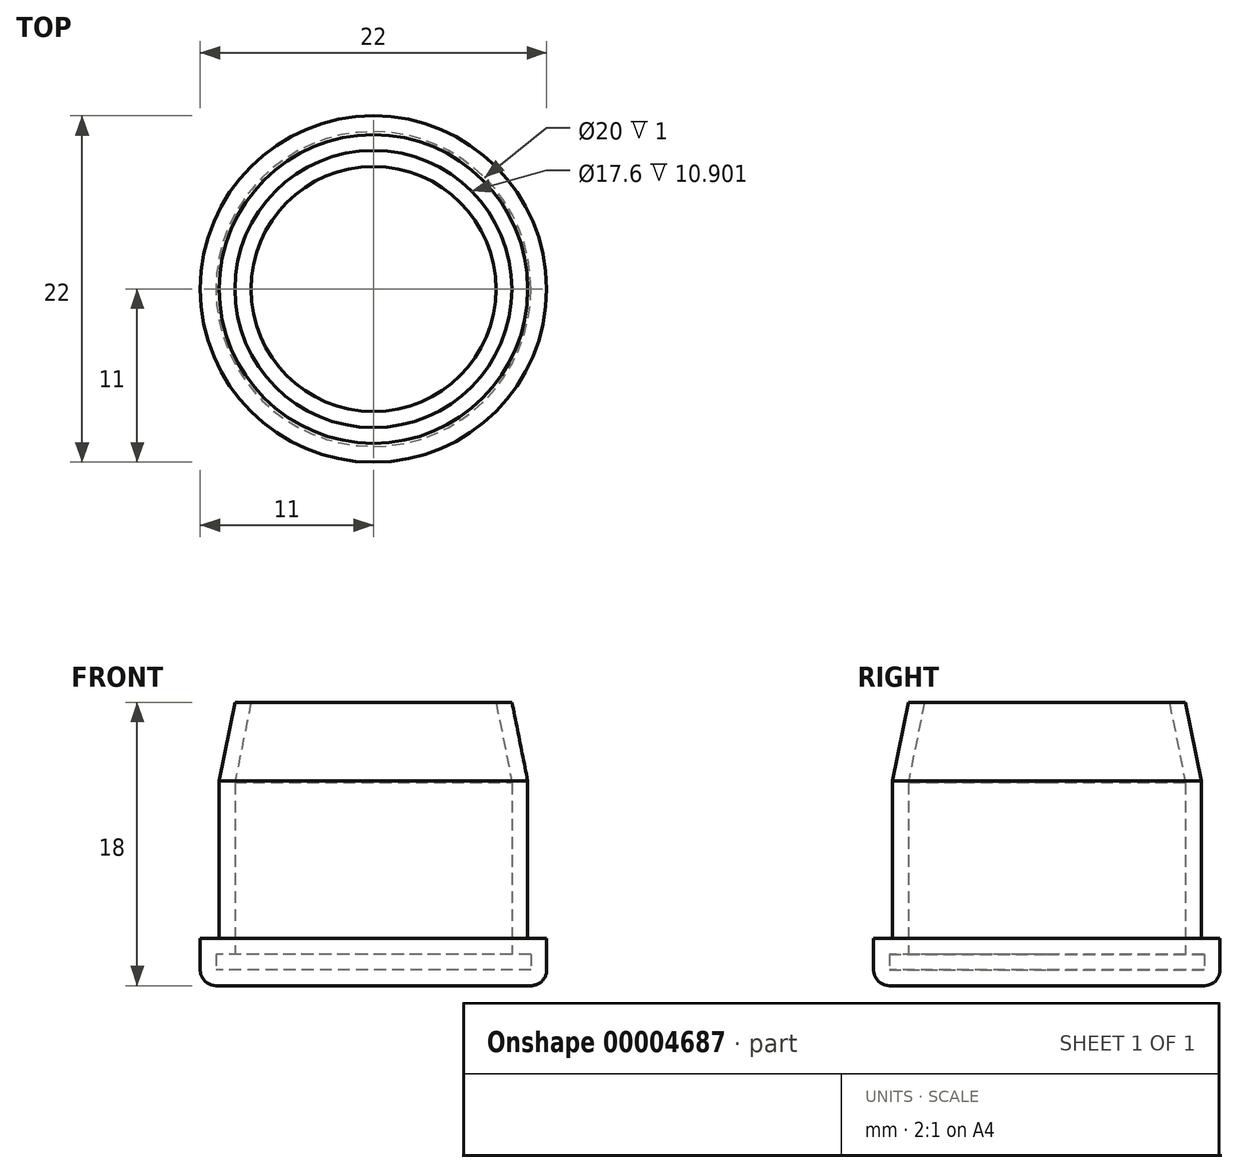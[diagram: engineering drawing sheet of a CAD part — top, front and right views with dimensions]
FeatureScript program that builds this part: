
annotation { "Feature Type Name" : "Feature", "Feature Type Description" : "" }
export const myFeature = defineFeature(function(context is Context, id is Id, definition is map)
    precondition{}
    {
        {
            var Q0;
            Q0=qCreatedBy(makeId("Top.planeOp"),FACE);
            var sketch = newSketch(context, id + "F0", { "sketchPlane" : qUnion([Q0])});
            skCircle(sketch, "E0", {"center": v(0, 0) * mm, "radius": 11 * mm});
            skSolve(sketch);
        }
        {
            var Q0;
            Q0 = qSketchRegion(id + "F0", true);
            extrude(context, id + "F1", {"entities" : qUnion([Q0]), "depth" : 3 * mm});
        }
        {
            var Q0;
            Q0=makeQuery(id+"F1.opExtrude","CAP_FACE",FACE,{"disambiguationData":[OSD([sQuery(id+"F0.wireOp",EDGE,"E0")])],"isStart":false});
            var sketch = newSketch(context, id + "F2", { "sketchPlane" : qUnion([Q0])});
            skCircle(sketch, "E1", {"center": v(0, 0) * mm, "radius": 9.8 * mm});
            skSolve(sketch);
        }
        {
            var Q0;
            Q0 = qSketchRegion(id + "F2", true);
            extrude(context, id + "F3", {"entities" : qUnion([Q0]), "operationType" : NewBodyOperationType.ADD, "depth" : 15 * mm});
        }
        {
            var Q0;
            Q0=makeQuery(id+"F3.opExtrude","CAP_EDGE",EDGE,{"disambiguationData":[OSD([sQuery(id+"F2.wireOp",EDGE,"E1")])],"isStart":false});
            chamfer(context, id + "F4", {"entities" : qUnion([Q0]), "chamferType" : ChamferType.TWO_OFFSETS, "width1" : 1 * mm, "oppositeDirection" : false, "width2" : 5 * mm, "tangentPropagation" : true});
        }
        {
            var Q0;
            Q0=makeQuery(id+"F3.opExtrude","CAP_FACE",FACE,{"disambiguationData":[OSD([sQuery(id+"F2.wireOp",EDGE,"E1")])],"isStart":false});
            shell(context, id + "F5", {"entities" : qUnion([Q0]), "thickness" : 1 * mm});
        }
        {
            var Q0;
            Q0=makeQuery(id+"F1.opExtrude","CAP_EDGE",EDGE,{"disambiguationData":[OSD([sQuery(id+"F0.wireOp",EDGE,"E0")])],"isStart":true});
            fillet(context, id + "F6", {"entities" : qUnion([Q0]), "radius" : 1 * mm, "tangentPropagation" : true, "allowEdgeOverflow" : false});
        }
    });
